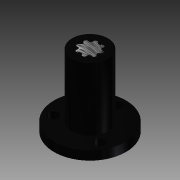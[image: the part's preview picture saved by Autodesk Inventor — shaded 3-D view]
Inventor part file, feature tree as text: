
AUTODESK INVENTOR PART (.ipt)
format: ipt  version: 2013 (Build 170138000, 138)  size: 2,112,512 bytes
history: native  units: mm
features: other x2, thread x1
ambient origin geometry x8: Origin, YZ Plane, XZ Plane, XY Plane, X Axis, Y Axis, Z Axis, Center Point
bodies: Solid1 (feature_tree)
feature tree (3):
  other  "LEAD NUT ASSEMBLY.iam"
  other  "LEAD NUT BLANK.ipt:1"
  thread  "thread.ipt:1"  [1 undecoded]
note: 1 required parameter value undecoded (feature->parameter linkage not recoverable at this tier; creation-order binding heuristic only, values carry confidence <= 0.55)
